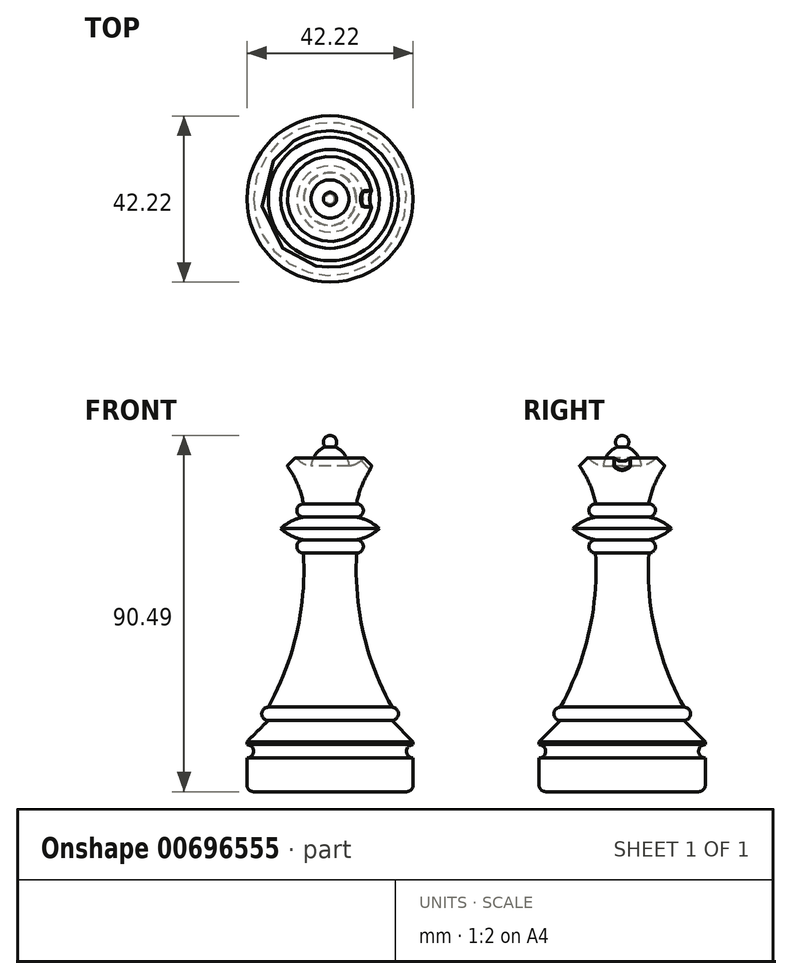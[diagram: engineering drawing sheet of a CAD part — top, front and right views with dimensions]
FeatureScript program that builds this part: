
annotation { "Feature Type Name" : "Feature", "Feature Type Description" : "" }
export const myFeature = defineFeature(function(context is Context, id is Id, definition is map)
    precondition{}
    {
        {
            var Q0;
            Q0=qCreatedBy(makeId("Front.planeOp"),FACE);
            var sketch = newSketch(context, id + "F0", { "sketchPlane" : qUnion([Q0])});
            skLineSegment(sketch, "E0", {"start": v(0, 0) * mm, "end": v(16.51, 0) * mm});
            skLineSegment(sketch, "E1", {"start": v(16.51, 0) * mm, "end": v(22.23, -5.71) * mm});
            skLineSegment(sketch, "E2", {"start": v(22.23, -5.71) * mm, "end": v(22.23, -6.48) * mm});
            skArc(sketch, "E3", {"start": v(22.23, -6.48) * mm, "mid": v(20.45, -8.25) * mm, "end": v(22.23, -10.03) * mm});
            skLineSegment(sketch, "E4", {"start": v(22.23, -10.03) * mm, "end": v(22.23, -19.05) * mm});
            skLineSegment(sketch, "E5", {"start": v(22.23, -19.05) * mm, "end": v(0, -19.05) * mm});
            skLineSegment(sketch, "E6", {"start": v(0, -19.05) * mm, "end": v(0, 0) * mm});
            skSolve(sketch);
        }
        {
            var Q0;
            Q0=makeQuery(id+"F0.imprint","IMPRINT",FACE,{"disambiguationData":[TD([[makeQuery(id+"F0.imprint","IMPRINT",EDGE,{"derivedFrom":sQuery(id+"F0.wireOp",EDGE,"E0")}),-1.0]])]});
            var Q1;
            Q1=sQuery(id+"F0.wireOp",EDGE,"E6");
            revolve(context, id + "F1", {"entities" : qUnion([Q0]), "axis" : qUnion([Q1]), "revolveType" : RevolveType.FULL});
        }
        {
            var Q0;
            Q0=qCreatedBy(makeId("Front.planeOp"),FACE);
            var sketch = newSketch(context, id + "F2", { "sketchPlane" : qUnion([Q0])});
            skLineSegment(sketch, "E7", {"start": v(0, 76.2) * mm, "end": v(0, 0) * mm});
            skLineSegment(sketch, "E8", {"start": v(0, 0) * mm, "end": v(16.51, 0) * mm});
            skArc(sketch, "E9", {"start": v(16.51, 0) * mm, "mid": v(18.29, 1.78) * mm, "end": v(16.51, 3.56) * mm});
            skArc(sketch, "E10", {"start": v(7.11, 44.73) * mm, "mid": v(8.9, 23.48) * mm, "end": v(16.5, 3.56) * mm});
            skArc(sketch, "E11", {"start": v(7.11, 44.73) * mm, "mid": v(8.9, 46.5) * mm, "end": v(7.11, 48.29) * mm});
            skArc(sketch, "E12", {"start": v(7.11, 48.29) * mm, "mid": v(10.37, 49.4) * mm, "end": v(13.2, 51.33) * mm});
            skArc(sketch, "E13", {"start": v(13.2, 51.33) * mm, "mid": v(10.37, 53.27) * mm, "end": v(7.11, 54.38) * mm});
            skArc(sketch, "E14", {"start": v(7.11, 54.38) * mm, "mid": v(8.9, 56.16) * mm, "end": v(7.11, 57.94) * mm});
            skArc(sketch, "E15", {"start": v(11.43, 68.1) * mm, "mid": v(8.71, 63.26) * mm, "end": v(7.11, 57.94) * mm});
            skLineSegment(sketch, "E16", {"start": v(11.43, 68.1) * mm, "end": v(9.18, 70.34) * mm});
            skArc(sketch, "E17", {"start": v(5.08, 68.1) * mm, "mid": v(7.35, 68.83) * mm, "end": v(9.18, 70.34) * mm});
            skArc(sketch, "E18", {"start": v(5.08, 68.1) * mm, "mid": v(3.86, 71.15) * mm, "end": v(1.27, 73.18) * mm});
            skArc(sketch, "E19", {"start": v(1.27, 73.18) * mm, "mid": v(1.64, 75.11) * mm, "end": v(0, 76.2) * mm});
            skLineSegment(sketch, "E20", {"start": v(7.11, 54.38) * mm, "end": v(7.11, 48.29) * mm, "construction": true});
            skLineSegment(sketch, "E21", {"start": v(13.2, 51.33) * mm, "end": v(7.11, 51.33) * mm, "construction": true});
            skSolve(sketch);
        }
        {
            var Q0;
            Q0=makeQuery(id+"F2.imprint","IMPRINT",FACE,{"disambiguationData":[TD([[makeQuery(id+"F2.imprint","IMPRINT",EDGE,{"derivedFrom":sQuery(id+"F2.wireOp",EDGE,"E7")}),1.0]])]});
            var Q1;
            Q1=sQuery(id+"F2.wireOp",EDGE,"E7");
            revolve(context, id + "F3", {"operationType" : NewBodyOperationType.ADD, "entities" : qUnion([Q0]), "axis" : qUnion([Q1]), "revolveType" : RevolveType.FULL});
        }
        {
            var Q0;
            Q0=sQuery(id+"F2.wireOp",VERTEX,"E15.start");
            var Q1;
            Q1=sQuery(id+"F2.wireOp",EDGE,"E16");
            cPlane(context, id + "F4", {"entities" : qUnion([Q0, Q1]), "cplaneType" : CPlaneType.LINE_POINT, "offset" : 25.4 * mm, "width" : 152.4 * mm, "height" : 152.4 * mm});
        }
        {
            var Q0;
            Q0=qCreatedBy(id+"F4.planeOp",FACE);
            var sketch = newSketch(context, id + "F5", { "sketchPlane" : qUnion([Q0])});
            skCircle(sketch, "E22", {"center": v(0, 57.5) * mm, "radius": 2.54 * mm});
            skSolve(sketch);
        }
        {
            var Q0;
            Q0=qSketchRegion(id+"F5",true);
            extrude(context, id + "F6", {"entities" : qUnion([Q0]), "operationType" : NewBodyOperationType.REMOVE, "depth" : 5.08 * mm, "hasSecondDirection" : true, "secondDirectionOppositeDirection" : true, "secondDirectionDepth" : 5.08 * mm});
        }
        {
            var Q0;
            Q0=makeQuery(id+"F6.boolean.opBoolean","INTERSECT",EDGE,{"disambiguationData":[OD(1.0)],"derivedFrom":[makeQuery(id+"F3.opRevolve","SWEPT_FACE",FACE,{"disambiguationData":[OSD([sQuery(id+"F2.wireOp",EDGE,"E16")])]}),makeQuery(id+"F6.opExtrude","SWEPT_FACE",FACE,{"disambiguationData":[OSD([sQuery(id+"F5.wireOp",EDGE,"E22")])]})]});
            var Q1;
            Q1=makeQuery(id+"F6.boolean.opBoolean","INTERSECT",EDGE,{"disambiguationData":[OD(0.0)],"derivedFrom":[makeQuery(id+"F3.opRevolve","SWEPT_FACE",FACE,{"disambiguationData":[OSD([sQuery(id+"F2.wireOp",EDGE,"E16")])]}),makeQuery(id+"F6.opExtrude","SWEPT_FACE",FACE,{"disambiguationData":[OSD([sQuery(id+"F5.wireOp",EDGE,"E22")])]})]});
            fillet(context, id + "F7", {"entities" : qUnion([Q0, Q1]), "radius" : 0.2 * mm, "tangentPropagation" : true, "allowEdgeOverflow" : false});
        }
        {
            var Q0;
            Q0=makeQuery(id+"F6.boolean.opBoolean","INTERSECT",EDGE,{"derivedFrom":[makeQuery(id+"F3.opRevolve","SWEPT_FACE",FACE,{"disambiguationData":[OSD([sQuery(id+"F2.wireOp",EDGE,"E17")])]}),makeQuery(id+"F6.opExtrude","SWEPT_FACE",FACE,{"disambiguationData":[OSD([sQuery(id+"F5.wireOp",EDGE,"E22")])]})]});
            var Q1;
            Q1=makeQuery(id+"F6.boolean.opBoolean","INTERSECT",EDGE,{"derivedFrom":[makeQuery(id+"F3.opRevolve","SWEPT_FACE",FACE,{"disambiguationData":[OSD([sQuery(id+"F2.wireOp",EDGE,"E15")])]}),makeQuery(id+"F6.opExtrude","SWEPT_FACE",FACE,{"disambiguationData":[OSD([sQuery(id+"F5.wireOp",EDGE,"E22")])]})]});
            fillet(context, id + "F8", {"entities" : qUnion([Q0, Q1]), "radius" : 0.2 * mm, "tangentPropagation" : true, "allowEdgeOverflow" : false});
        }
        {
            var Q0;
            Q0=makeQuery(id+"F1.opRevolve","SWEPT_EDGE",EDGE,{"disambiguationData":[OSD([sQuery(id+"F0.wireOp",EDGE,"E4"),sQuery(id+"F0.wireOp",EDGE,"E5")])]});
            fillet(context, id + "F9", {"entities" : qUnion([Q0]), "radius" : 1.78 * mm, "tangentPropagation" : true, "allowEdgeOverflow" : false});
        }
        {
            var Q0;
            Q0=makeQuery(id+"F1.opRevolve","SWEPT_BODY",BODY,{"disambiguationData":[OSD([sQuery(id+"F0.wireOp",EDGE,"E0"),sQuery(id+"F0.wireOp",EDGE,"E1"),sQuery(id+"F0.wireOp",EDGE,"E2"),sQuery(id+"F0.wireOp",EDGE,"E3"),sQuery(id+"F0.wireOp",EDGE,"E4"),sQuery(id+"F0.wireOp",EDGE,"E5"),sQuery(id+"F0.wireOp",EDGE,"E6")])]});
            var Q1;
            Q1=qCreatedBy(makeId("Origin.pointOp"),VERTEX);
            transform(context, id + "F10", {"entities" : qUnion([Q0]), "transformType" : TransformType.SCALE_UNIFORMLY, "scale" : .95, "scalePoint" : qUnion([Q1]), "makeCopy" : false});
        }
    });
